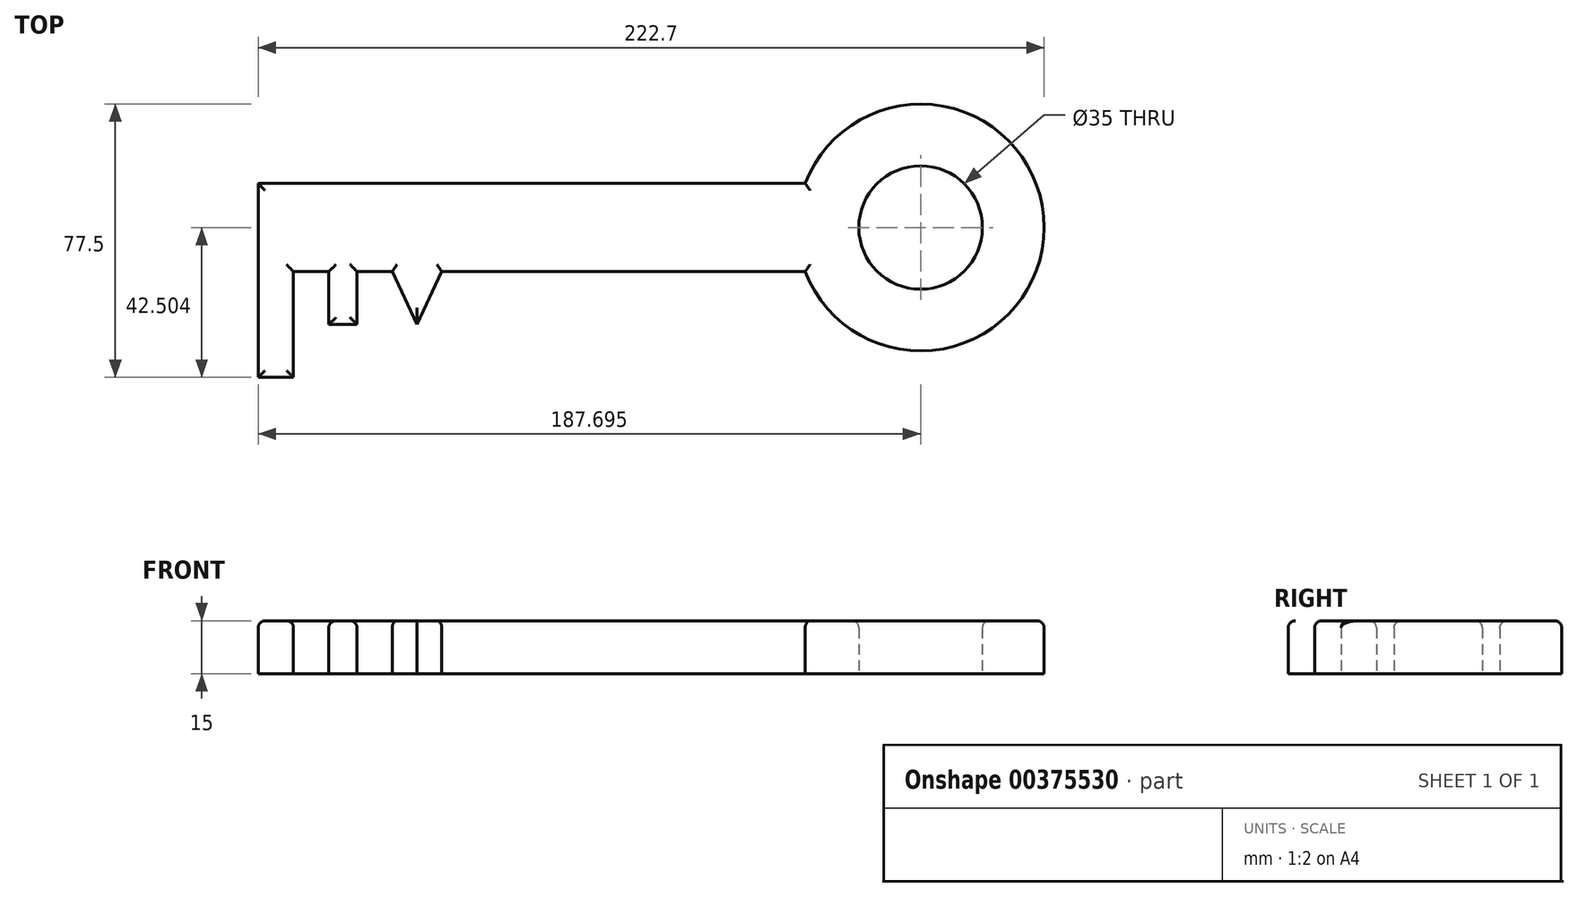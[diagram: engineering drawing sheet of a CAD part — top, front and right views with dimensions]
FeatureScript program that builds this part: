
annotation { "Feature Type Name" : "Feature", "Feature Type Description" : "" }
export const myFeature = defineFeature(function(context is Context, id is Id, definition is map)
    precondition{}
    {
        {
            var Q0;
            Q0=qCreatedBy(makeId("Top.planeOp"),FACE);
            var sketch = newSketch(context, id + "F0", { "sketchPlane" : qUnion([Q0])});
            skLineSegment(sketch, "E0.top", {"start": v(-89.47, -12.06) * mm, "end": v(-79.47, -12.06) * mm});
            skLineSegment(sketch, "E0.left", {"start": v(-89.47, 17.94) * mm, "end": v(-89.47, -12.06) * mm});
            skLineSegment(sketch, "E0.right", {"start": v(-79.47, 17.94) * mm, "end": v(-79.47, -12.06) * mm});
            skLineSegment(sketch, "E1.top", {"start": v(-69.47, 2.94) * mm, "end": v(-61.47, 2.94) * mm});
            skLineSegment(sketch, "E1.left", {"start": v(-69.47, 17.94) * mm, "end": v(-69.47, 2.94) * mm});
            skLineSegment(sketch, "E1.right", {"start": v(-61.47, 17.94) * mm, "end": v(-61.47, 2.94) * mm});
            skLineSegment(sketch, "E2", {"start": v(-51.47, 17.94) * mm, "end": v(-44.47, 2.94) * mm});
            skLineSegment(sketch, "E3", {"start": v(-44.47, 2.94) * mm, "end": v(-37.47, 17.94) * mm});
            skLineSegment(sketch, "E4", {"start": v(-44.47, 2.94) * mm, "end": v(-44.47, 17.94) * mm, "construction": true});
            skLineSegment(sketch, "E5.bottom", {"start": v(-79.47, 17.94) * mm, "end": v(-69.47, 17.94) * mm});
            skLineSegment(sketch, "E5.top", {"start": v(-89.47, 42.94) * mm, "end": v(65.53, 42.94) * mm});
            skLineSegment(sketch, "E5.left", {"start": v(-89.47, 17.94) * mm, "end": v(-89.47, 42.94) * mm});
            skArc(sketch, "E6", {"start": v(65.53, 17.94) * mm, "mid": v(133.23, 30.44) * mm, "end": v(65.53, 42.94) * mm});
            skCircle(sketch, "E7", {"center": v(98.23, 30.44) * mm, "radius": 17.5 * mm});
            skLineSegment(sketch, "E8", {"start": v(98.23, 30.44) * mm, "end": v(-89.47, 30.44) * mm, "construction": true});
            skLineSegment(sketch, "E9.trimOffspring", {"start": v(-37.47, 17.94) * mm, "end": v(65.53, 17.94) * mm});
            skLineSegment(sketch, "E10.trimOffspring", {"start": v(-61.47, 17.94) * mm, "end": v(-51.47, 17.94) * mm});
            skSolve(sketch);
        }
        {
            var Q0;
            Q0=makeQuery(id+"F0.imprint","IMPRINT",FACE,{"disambiguationData":[TD([[makeQuery(id+"F0.imprint","IMPRINT",EDGE,{"derivedFrom":sQuery(id+"F0.wireOp",EDGE,"E0.top")}),1.0]])]});
            extrude(context, id + "F1", {"entities" : qUnion([Q0]), "depth" : 15 * mm});
        }
        {
            var Q0;
            Q0=makeQuery(id+"F1.opExtrude","CAP_EDGE",EDGE,{"disambiguationData":[OSD([sQuery(id+"F0.wireOp",EDGE,"E0.left"),sQuery(id+"F0.wireOp",EDGE,"E5.left")])],"isStart":false});
            var Q1;
            Q1=makeQuery(id+"F1.opExtrude","CAP_EDGE",EDGE,{"disambiguationData":[OSD([sQuery(id+"F0.wireOp",EDGE,"E5.top")])],"isStart":false});
            var Q2;
            Q2=makeQuery(id+"F1.opExtrude","CAP_EDGE",EDGE,{"disambiguationData":[OSD([sQuery(id+"F0.wireOp",EDGE,"E6")])],"isStart":false});
            var Q3;
            Q3=makeQuery(id+"F1.opExtrude","CAP_EDGE",EDGE,{"disambiguationData":[OSD([sQuery(id+"F0.wireOp",EDGE,"E9.trimOffspring")])],"isStart":false});
            var Q4;
            Q4=makeQuery(id+"F1.opExtrude","CAP_EDGE",EDGE,{"disambiguationData":[OSD([sQuery(id+"F0.wireOp",EDGE,"E3")])],"isStart":false});
            var Q5;
            Q5=makeQuery(id+"F1.opExtrude","CAP_FACE",FACE,{"disambiguationData":[OSD([sQuery(id+"F0.wireOp",EDGE,"E0.top"),sQuery(id+"F0.wireOp",EDGE,"E0.left"),sQuery(id+"F0.wireOp",EDGE,"E0.right"),sQuery(id+"F0.wireOp",EDGE,"E1.top"),sQuery(id+"F0.wireOp",EDGE,"E1.left"),sQuery(id+"F0.wireOp",EDGE,"E1.right"),sQuery(id+"F0.wireOp",EDGE,"E2"),sQuery(id+"F0.wireOp",EDGE,"E3"),sQuery(id+"F0.wireOp",EDGE,"E5.bottom"),sQuery(id+"F0.wireOp",EDGE,"E5.top"),sQuery(id+"F0.wireOp",EDGE,"E5.left"),sQuery(id+"F0.wireOp",EDGE,"E6"),sQuery(id+"F0.wireOp",EDGE,"E7"),sQuery(id+"F0.wireOp",EDGE,"E9.trimOffspring"),sQuery(id+"F0.wireOp",EDGE,"E10.trimOffspring")])],"isStart":false});
            var Q6;
            Q6=makeQuery(id+"F1.opExtrude","CAP_EDGE",EDGE,{"disambiguationData":[OSD([sQuery(id+"F0.wireOp",EDGE,"E0.right")])],"isStart":false});
            fillet(context, id + "F2", {"entities" : qUnion([Q0, Q1, Q2, Q3, Q4, Q5, Q6]), "radius" : 2 * mm, "tangentPropagation" : true, "allowEdgeOverflow" : false});
        }
    });
